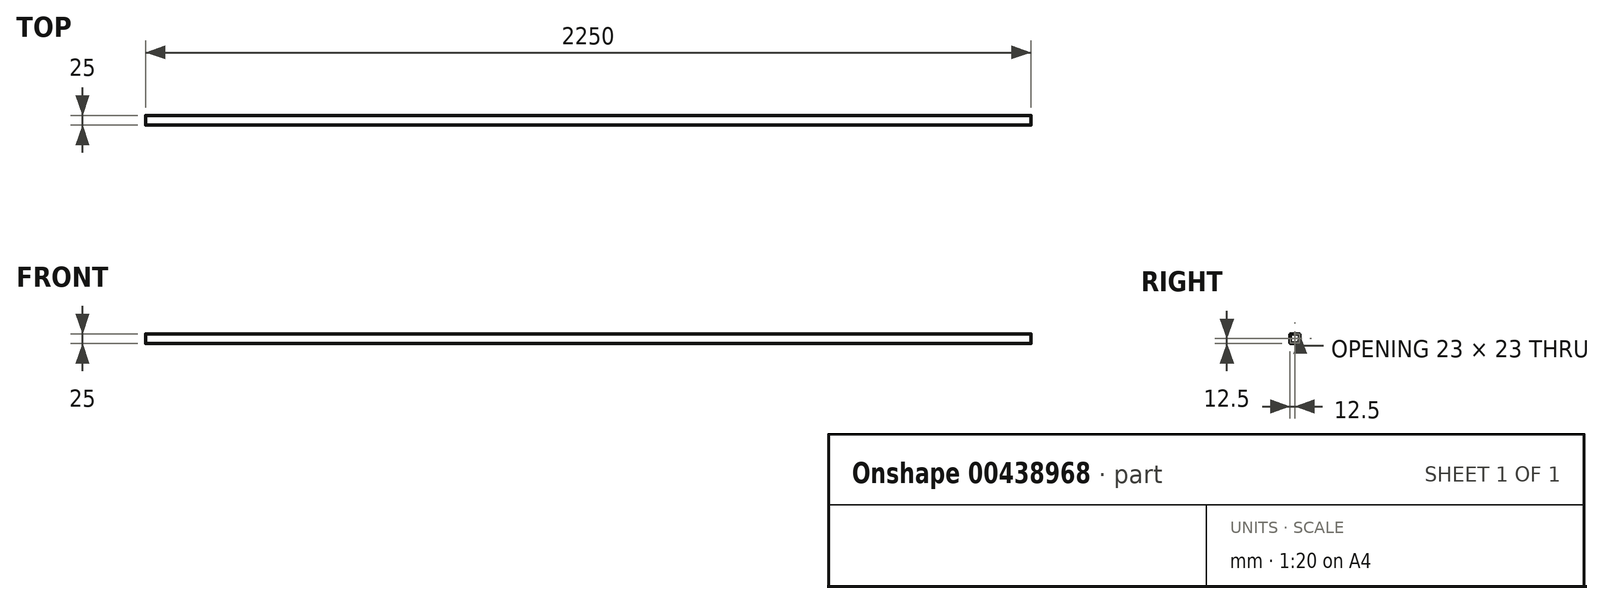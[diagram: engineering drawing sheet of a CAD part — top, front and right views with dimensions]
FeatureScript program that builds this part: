
annotation { "Feature Type Name" : "Feature", "Feature Type Description" : "" }
export const myFeature = defineFeature(function(context is Context, id is Id, definition is map)
    precondition{}
    {
        {
            var Q0;
            Q0=qCreatedBy(makeId("Right.planeOp"),FACE);
            var sketch = newSketch(context, id + "F0", { "sketchPlane" : qUnion([Q0])});
            skLineSegment(sketch, "E0.bottom", {"start": v(10.5, 12.5) * mm, "end": v(-10.5, 12.5) * mm});
            skLineSegment(sketch, "E0.top", {"start": v(10.5, -12.5) * mm, "end": v(-10.5, -12.5) * mm});
            skLineSegment(sketch, "E0.left", {"start": v(12.5, 10.5) * mm, "end": v(12.5, -10.5) * mm});
            skLineSegment(sketch, "E0.right", {"start": v(-12.5, 10.5) * mm, "end": v(-12.5, -10.5) * mm});
            skPoint(sketch, "E0.middle", {"position": v(0, 0) * mm});
            skLineSegment(sketch, "E1.bottom", {"start": v(9.5, 11.5) * mm, "end": v(-9.5, 11.5) * mm});
            skLineSegment(sketch, "E1.top", {"start": v(9.5, -11.5) * mm, "end": v(-9.5, -11.5) * mm});
            skLineSegment(sketch, "E1.left", {"start": v(11.5, 9.5) * mm, "end": v(11.5, -9.5) * mm});
            skLineSegment(sketch, "E1.right", {"start": v(-11.5, 9.5) * mm, "end": v(-11.5, -9.5) * mm});
            skPoint(sketch, "E2.visualSharp", {"position": v(-12.5, 12.5) * mm});
            skArc(sketch, "E2.filletArc", {"start": v(-10.5, 12.5) * mm, "mid": v(-11.91, 11.91) * mm, "end": v(-12.5, 10.5) * mm});
            skPoint(sketch, "E3.visualSharp", {"position": v(-11.5, 11.5) * mm});
            skArc(sketch, "E3.filletArc", {"start": v(-9.5, 11.5) * mm, "mid": v(-10.91, 10.91) * mm, "end": v(-11.5, 9.5) * mm});
            skPoint(sketch, "E4.visualSharp", {"position": v(12.5, 12.5) * mm});
            skArc(sketch, "E4.filletArc", {"start": v(12.5, 10.5) * mm, "mid": v(11.91, 11.91) * mm, "end": v(10.5, 12.5) * mm});
            skPoint(sketch, "E5.visualSharp", {"position": v(11.5, 11.5) * mm});
            skArc(sketch, "E5.filletArc", {"start": v(11.5, 9.5) * mm, "mid": v(10.91, 10.91) * mm, "end": v(9.5, 11.5) * mm});
            skPoint(sketch, "E6.visualSharp", {"position": v(12.5, -12.5) * mm});
            skArc(sketch, "E6.filletArc", {"start": v(10.5, -12.5) * mm, "mid": v(11.91, -11.91) * mm, "end": v(12.5, -10.5) * mm});
            skPoint(sketch, "E7.visualSharp", {"position": v(11.5, -11.5) * mm});
            skArc(sketch, "E7.filletArc", {"start": v(9.5, -11.5) * mm, "mid": v(10.91, -10.91) * mm, "end": v(11.5, -9.5) * mm});
            skPoint(sketch, "E8.visualSharp", {"position": v(-11.5, -11.5) * mm});
            skArc(sketch, "E8.filletArc", {"start": v(-11.5, -9.5) * mm, "mid": v(-10.91, -10.91) * mm, "end": v(-9.5, -11.5) * mm});
            skPoint(sketch, "E9.visualSharp", {"position": v(-12.5, -12.5) * mm});
            skArc(sketch, "E9.filletArc", {"start": v(-12.5, -10.5) * mm, "mid": v(-11.91, -11.91) * mm, "end": v(-10.5, -12.5) * mm});
            skSolve(sketch);
        }
        {
            var Q0;
            Q0=makeQuery(id+"F0.imprint","IMPRINT",FACE,{"disambiguationData":[TD([[makeQuery(id+"F0.imprint","IMPRINT",EDGE,{"derivedFrom":sQuery(id+"F0.wireOp",EDGE,"E0.bottom")}),1.0]])]});
            extrude(context, id + "F1", {"entities" : qUnion([Q0]), "endBound" : BoundingType.SYMMETRIC, "depth" : 2250 * mm});
        }
    });
